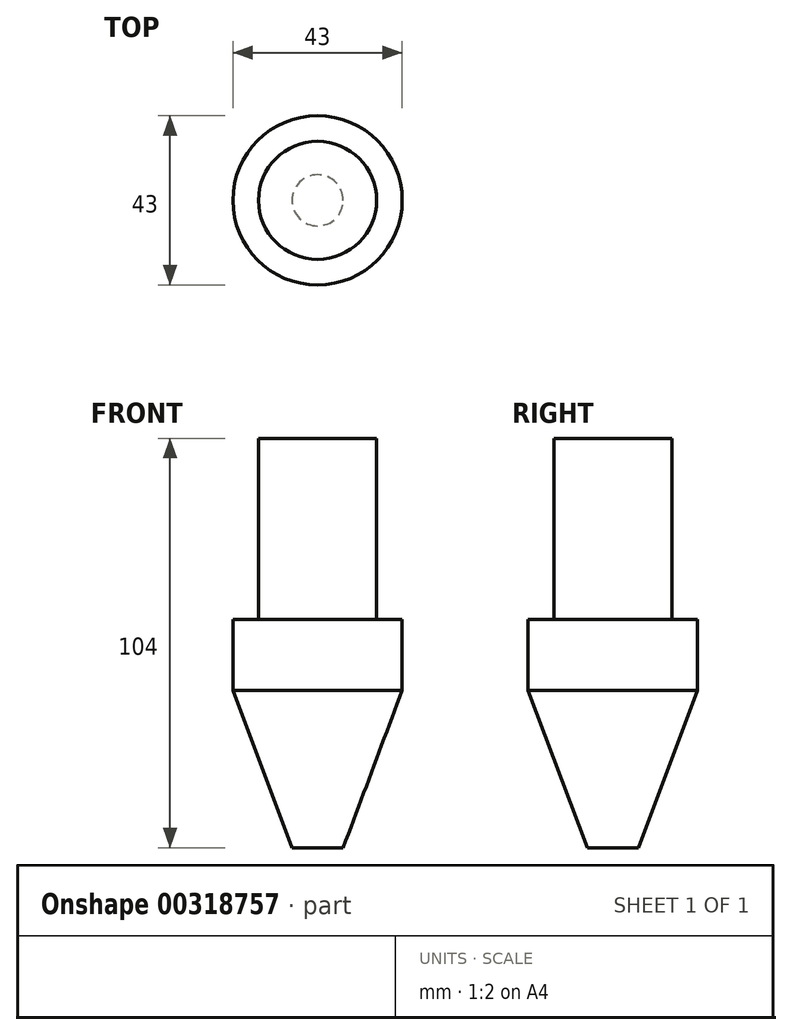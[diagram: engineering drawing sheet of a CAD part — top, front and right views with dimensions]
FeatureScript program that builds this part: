
annotation { "Feature Type Name" : "Feature", "Feature Type Description" : "" }
export const myFeature = defineFeature(function(context is Context, id is Id, definition is map)
    precondition{}
    {
        {
            var Q0;
            Q0=qCreatedBy(makeId("Top.planeOp"),FACE);
            var sketch = newSketch(context, id + "F0", { "sketchPlane" : qUnion([Q0])});
            skCircle(sketch, "E0", {"center": v(0, 0) * mm, "radius": 21.5 * mm});
            skSolve(sketch);
        }
        {
            var Q0;
            Q0=makeQuery(id+"F0.imprint","IMPRINT",FACE,{"disambiguationData":[TD([[makeQuery(id+"F0.imprint","IMPRINT",EDGE,{"derivedFrom":sQuery(id+"F0.wireOp",EDGE,"E0")}),1.0]])]});
            extrude(context, id + "F1", {"entities" : qUnion([Q0]), "depth" : 58 * mm, "offsetDistance" : 25 * mm});
        }
        {
            var Q0;
            Q0=makeQuery(id+"F1.opExtrude","CAP_FACE",FACE,{"disambiguationData":[OSD([sQuery(id+"F0.wireOp",EDGE,"E0")])],"isStart":false});
            var sketch = newSketch(context, id + "F2", { "sketchPlane" : qUnion([Q0])});
            skCircle(sketch, "E1", {"center": v(0, 0) * mm, "radius": 15 * mm});
            skSolve(sketch);
        }
        {
            var Q0;
            Q0 = qSketchRegion(id + "F2", true);
            extrude(context, id + "F3", {"entities" : qUnion([Q0]), "operationType" : NewBodyOperationType.ADD, "depth" : 46 * mm, "offsetDistance" : 25 * mm});
        }
        {
            var Q0;
            Q0=makeQuery(id+"F1.opExtrude","CAP_FACE",FACE,{"disambiguationData":[OSD([sQuery(id+"F0.wireOp",EDGE,"E0")])],"isStart":true});
            chamfer(context, id + "F4", {"entities" : qUnion([Q0]), "chamferType" : ChamferType.TWO_OFFSETS, "width1" : 40 * mm, "oppositeDirection" : false, "width2" : 15 * mm, "tangentPropagation" : true});
        }
    });
